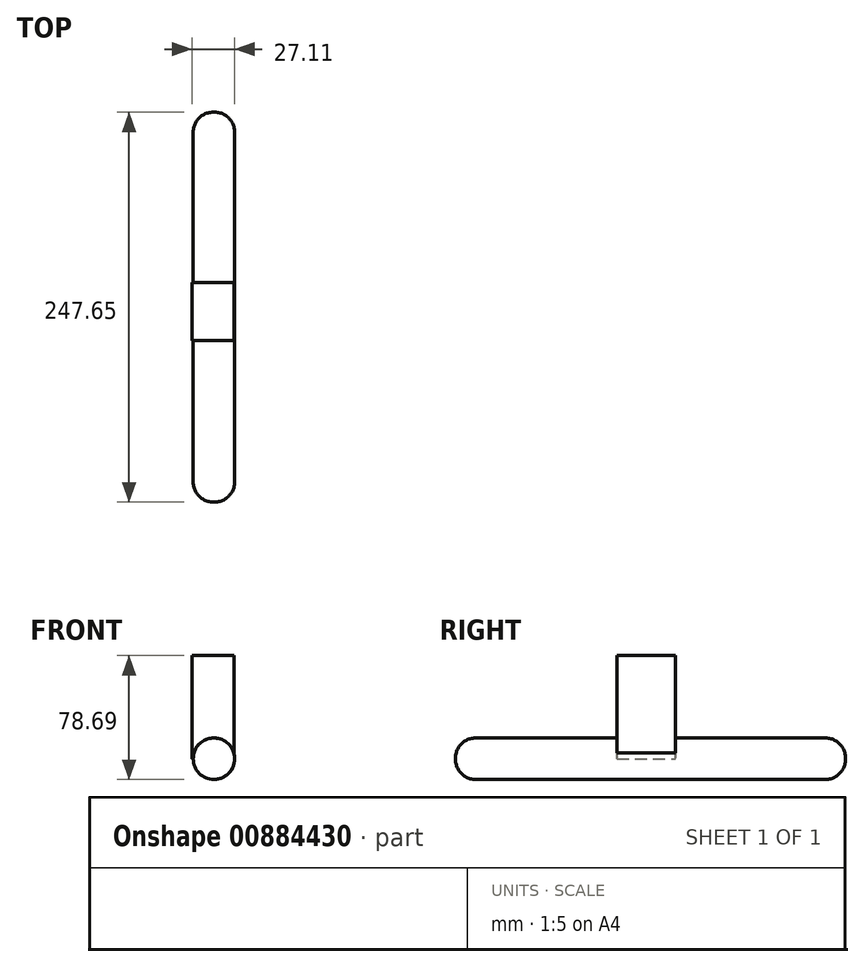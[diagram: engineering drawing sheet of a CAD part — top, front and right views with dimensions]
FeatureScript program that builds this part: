
annotation { "Feature Type Name" : "Feature", "Feature Type Description" : "" }
export const myFeature = defineFeature(function(context is Context, id is Id, definition is map)
    precondition{}
    {
        {
            var Q0;
            Q0=qCreatedBy(makeId("Front.planeOp"),FACE);
            var sketch = newSketch(context, id + "F0", { "sketchPlane" : qUnion([Q0])});
            skCircle(sketch, "E0", {"center": v(0, 0) * mm, "radius": 13.16 * mm});
            skSolve(sketch);
        }
        {
            var Q0;
            Q0 = qSketchRegion(id + "F0", true);
            extrude(context, id + "F1", {"entities" : qUnion([Q0]), "depth" : 247.65 * mm, "offsetDistance" : 25.4 * mm});
        }
        {
            var Q0;
            Q0=qCreatedBy(makeId("Top.planeOp"),FACE);
            var sketch = newSketch(context, id + "F2", { "sketchPlane" : qUnion([Q0])});
            skLineSegment(sketch, "E1.bottom", {"start": v(-13.95, -108.11) * mm, "end": v(12.65, -108.11) * mm});
            skLineSegment(sketch, "E1.top", {"start": v(-13.95, -145.1) * mm, "end": v(12.65, -145.1) * mm});
            skLineSegment(sketch, "E1.left", {"start": v(-13.95, -108.11) * mm, "end": v(-13.95, -145.1) * mm});
            skLineSegment(sketch, "E1.right", {"start": v(12.65, -108.11) * mm, "end": v(12.65, -145.1) * mm});
            skSolve(sketch);
        }
        {
            var Q0;
            Q0 = qSketchRegion(id + "F2", true);
            extrude(context, id + "F3", {"entities" : qUnion([Q0]), "operationType" : NewBodyOperationType.ADD, "depth" : 65.53 * mm, "offsetDistance" : 25.4 * mm});
        }
        {
            var Q0;
            Q0=makeQuery(id+"F1.opExtrude","CAP_EDGE",EDGE,{"disambiguationData":[OSD([sQuery(id+"F0.wireOp",EDGE,"E0")])],"isStart":false});
            fillet(context, id + "F4", {"entities" : qUnion([Q0]), "radius" : 12.7 * mm, "tangentPropagation" : true, "allowEdgeOverflow" : false});
        }
        {
            var Q0;
            Q0=makeQuery(id+"F1.opExtrude","CAP_EDGE",EDGE,{"disambiguationData":[OSD([sQuery(id+"F0.wireOp",EDGE,"E0")])],"isStart":true});
            fillet(context, id + "F5", {"entities" : qUnion([Q0]), "radius" : 12.7 * mm, "tangentPropagation" : true, "allowEdgeOverflow" : false});
        }
        {
            var Q0;
            Q0=qCreatedBy(makeId("Right.planeOp"),FACE);
            var sketch = newSketch(context, id + "F6", { "sketchPlane" : qUnion([Q0])});
            skLineSegment(sketch, "E2.bottom", {"start": v(-16.25, 3.82) * mm, "end": v(-230.32, 3.82) * mm});
            skLineSegment(sketch, "E2.top", {"start": v(-16.25, -3.82) * mm, "end": v(-230.32, -3.82) * mm});
            skLineSegment(sketch, "E2.left", {"start": v(-16.25, 3.82) * mm, "end": v(-16.25, -3.82) * mm});
            skLineSegment(sketch, "E2.right", {"start": v(-230.32, 3.82) * mm, "end": v(-230.32, -3.82) * mm});
            skSolve(sketch);
        }
        {
            var Q0;
            Q0 = qSketchRegion(id + "F6", true);
            extrude(context, id + "F7", {"entities" : qUnion([Q0]), "operationType" : NewBodyOperationType.ADD, "oppositeDirection" : true, "depth" : 11.43 * mm, "offsetDistance" : 25.4 * mm});
        }
        {
            var Q0;
            Q0=qCreatedBy(makeId("Right.planeOp"),FACE);
            var sketch = newSketch(context, id + "F8", { "sketchPlane" : qUnion([Q0])});
            skLineSegment(sketch, "E3.bottom", {"start": v(-16.7, 3.06) * mm, "end": v(-232.51, 3.06) * mm});
            skLineSegment(sketch, "E3.top", {"start": v(-16.7, -4.2) * mm, "end": v(-232.51, -4.2) * mm});
            skLineSegment(sketch, "E3.left", {"start": v(-16.7, 3.06) * mm, "end": v(-16.7, -4.2) * mm});
            skLineSegment(sketch, "E3.right", {"start": v(-232.51, 3.06) * mm, "end": v(-232.51, -4.2) * mm});
            skSolve(sketch);
        }
        {
            var Q0;
            Q0 = qSketchRegion(id + "F8", true);
            extrude(context, id + "F9", {"entities" : qUnion([Q0]), "operationType" : NewBodyOperationType.ADD, "depth" : 8.9 * mm, "offsetDistance" : 25.4 * mm});
        }
    });
